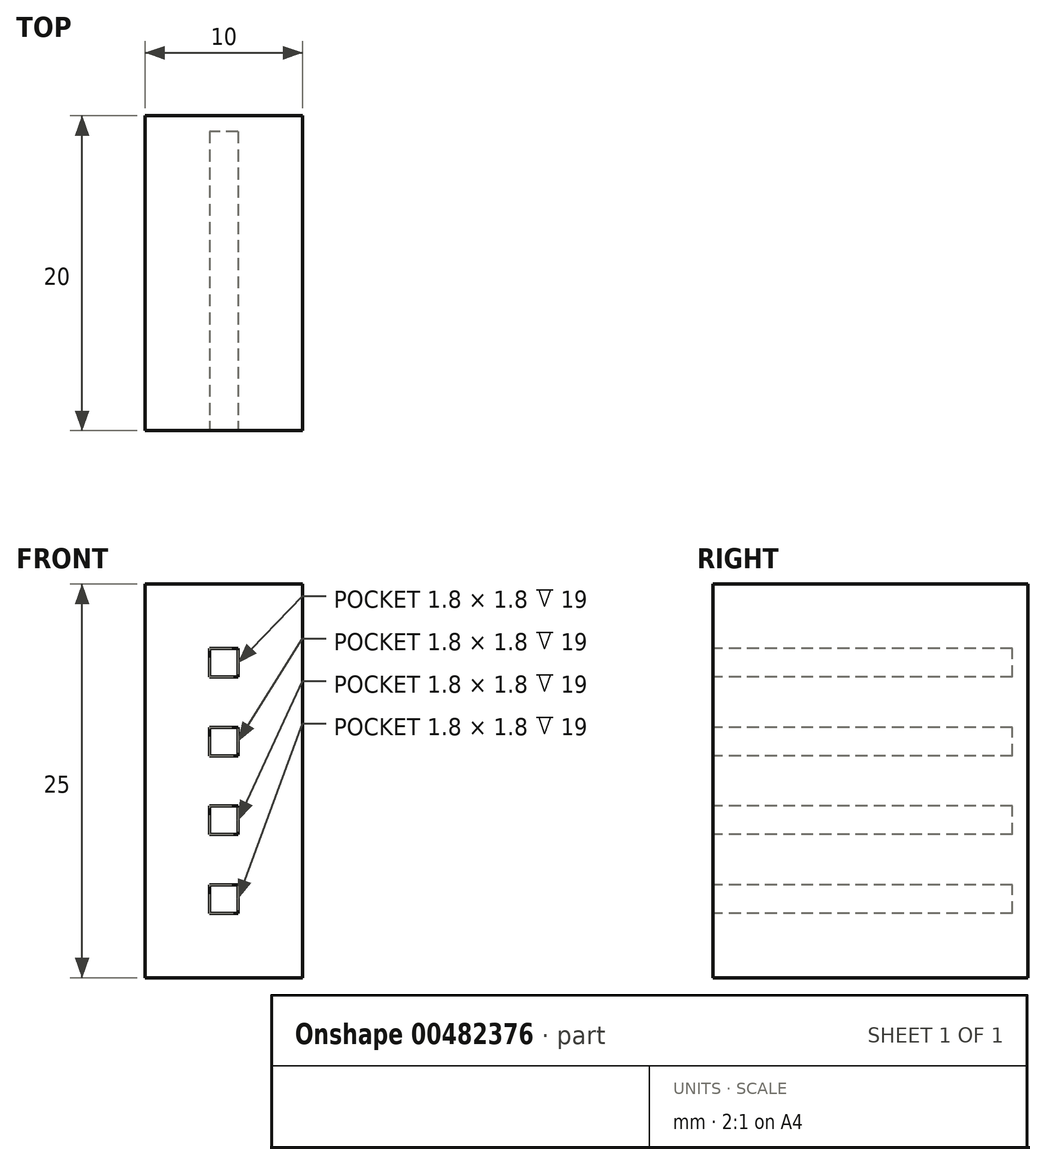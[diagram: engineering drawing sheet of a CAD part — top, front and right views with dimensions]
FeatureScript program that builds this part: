
annotation { "Feature Type Name" : "Feature", "Feature Type Description" : "" }
export const myFeature = defineFeature(function(context is Context, id is Id, definition is map)
    precondition{}
    {
        {
            var Q0;
            Q0=qCreatedBy(makeId("Top.planeOp"),FACE);
            var sketch = newSketch(context, id + "F0", { "sketchPlane" : qUnion([Q0])});
            skLineSegment(sketch, "E0.bottom", {"start": v(5, -10) * mm, "end": v(-5, -10) * mm});
            skLineSegment(sketch, "E0.top", {"start": v(5, 10) * mm, "end": v(-5, 10) * mm});
            skLineSegment(sketch, "E0.left", {"start": v(5, -10) * mm, "end": v(5, 10) * mm});
            skLineSegment(sketch, "E0.right", {"start": v(-5, -10) * mm, "end": v(-5, 10) * mm});
            skPoint(sketch, "E0.middle", {"position": v(0, 0) * mm});
            skSolve(sketch);
        }
        {
            var Q0;
            Q0 = qSketchRegion(id + "F0", true);
            extrude(context, id + "F1", {"entities" : qUnion([Q0]), "depth" : 25 * mm});
        }
        {
            var Q0;
            Q0=makeQuery(id+"F1.opExtrude","SWEPT_FACE",FACE,{"disambiguationData":[OSD([sQuery(id+"F0.wireOp",EDGE,"E0.bottom")])]});
            var sketch = newSketch(context, id + "F2", { "sketchPlane" : qUnion([Q0])});
            skLineSegment(sketch, "E1.bottom", {"start": v(0.9, 4.1) * mm, "end": v(-0.9, 4.1) * mm});
            skLineSegment(sketch, "E1.top", {"start": v(0.9, 5.9) * mm, "end": v(-0.9, 5.9) * mm});
            skLineSegment(sketch, "E1.left", {"start": v(0.9, 4.1) * mm, "end": v(0.9, 5.9) * mm});
            skLineSegment(sketch, "E1.right", {"start": v(-0.9, 4.1) * mm, "end": v(-0.9, 5.9) * mm});
            skPoint(sketch, "E1.middle", {"position": v(0, 5) * mm});
            skLineSegment(sketch, "E2.0.1.0", {"start": v(-0.9, 9.1) * mm, "end": v(-0.9, 10.9) * mm});
            skLineSegment(sketch, "E2.0.1.1", {"start": v(0.9, 9.1) * mm, "end": v(0.9, 10.9) * mm});
            skLineSegment(sketch, "E2.0.1.2", {"start": v(0.9, 10.9) * mm, "end": v(-0.9, 10.9) * mm});
            skLineSegment(sketch, "E2.0.1.3", {"start": v(0.9, 9.1) * mm, "end": v(-0.9, 9.1) * mm});
            skPoint(sketch, "E2.0.1.4", {"position": v(0, 10) * mm});
            skLineSegment(sketch, "E2.0.2.0", {"start": v(-0.9, 14.1) * mm, "end": v(-0.9, 15.9) * mm});
            skLineSegment(sketch, "E2.0.2.1", {"start": v(0.9, 14.1) * mm, "end": v(0.9, 15.9) * mm});
            skLineSegment(sketch, "E2.0.2.2", {"start": v(0.9, 15.9) * mm, "end": v(-0.9, 15.9) * mm});
            skLineSegment(sketch, "E2.0.2.3", {"start": v(0.9, 14.1) * mm, "end": v(-0.9, 14.1) * mm});
            skPoint(sketch, "E2.0.2.4", {"position": v(0, 15) * mm});
            skLineSegment(sketch, "E2.0.3.0", {"start": v(-0.9, 19.1) * mm, "end": v(-0.9, 20.9) * mm});
            skLineSegment(sketch, "E2.0.3.1", {"start": v(0.9, 19.1) * mm, "end": v(0.9, 20.9) * mm});
            skLineSegment(sketch, "E2.0.3.2", {"start": v(0.9, 20.9) * mm, "end": v(-0.9, 20.9) * mm});
            skLineSegment(sketch, "E2.0.3.3", {"start": v(0.9, 19.1) * mm, "end": v(-0.9, 19.1) * mm});
            skPoint(sketch, "E2.0.3.4", {"position": v(0, 20) * mm});
            skLineSegment(sketch, "E2.direction1", {"start": v(-0.9, 4.1) * mm, "end": v(18.5, 4.1) * mm, "construction": true});
            skLineSegment(sketch, "E2.direction2", {"start": v(-0.9, 4.1) * mm, "end": v(-0.9, 9.1) * mm, "construction": true});
            skSolve(sketch);
        }
        {
            var Q0;
            Q0 = qSketchRegion(id + "F2", true);
            extrude(context, id + "F3", {"entities" : qUnion([Q0]), "operationType" : NewBodyOperationType.REMOVE, "oppositeDirection" : true, "depth" : 19 * mm});
        }
    });
